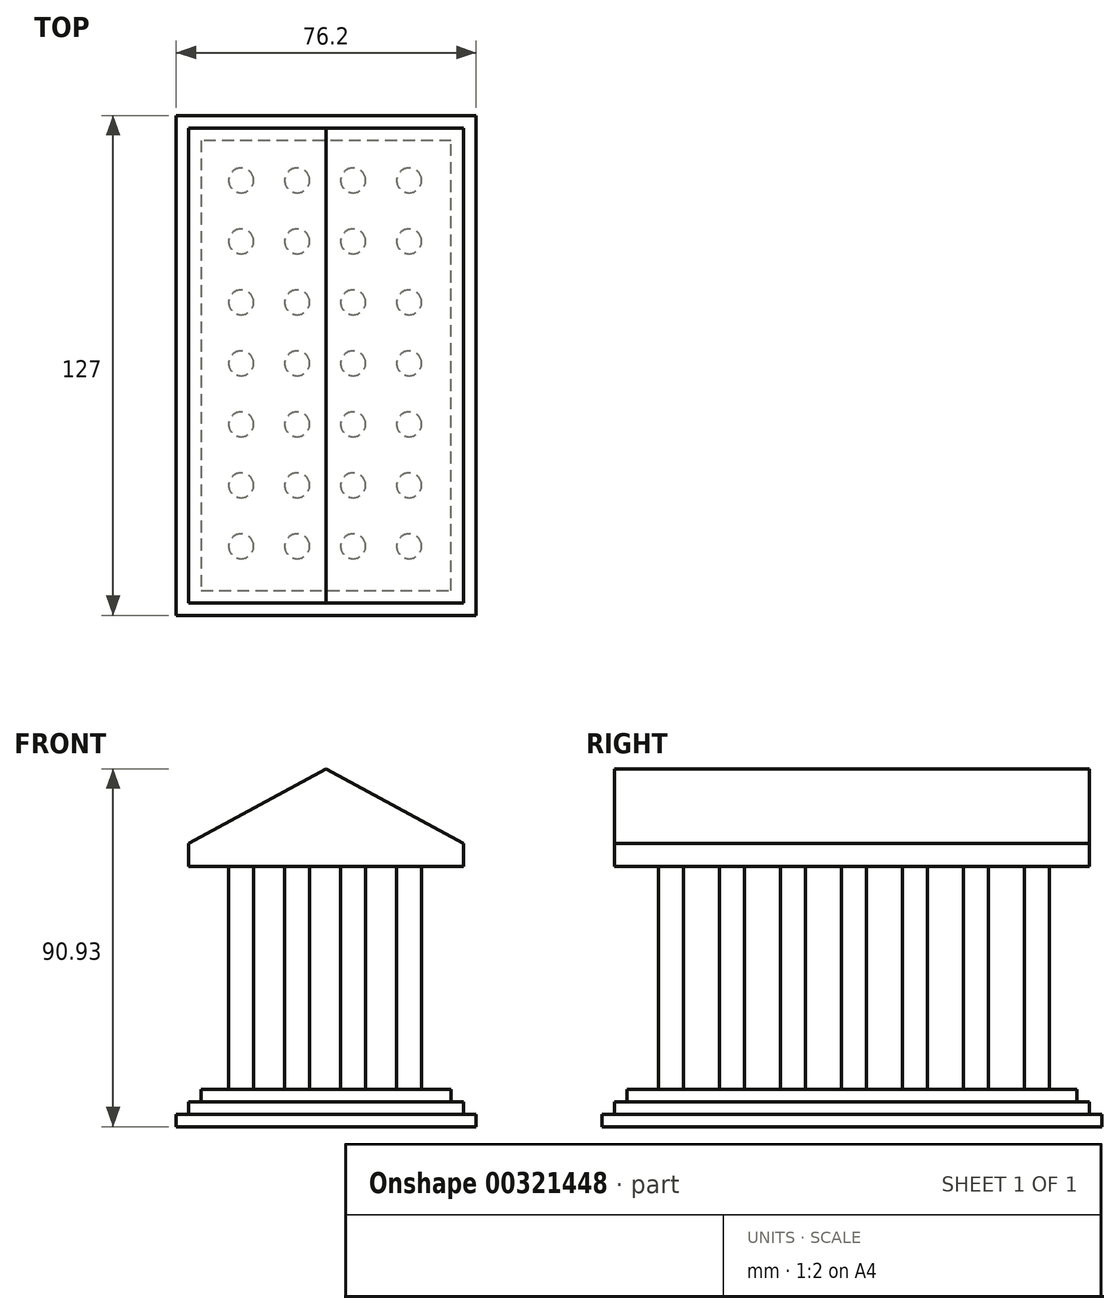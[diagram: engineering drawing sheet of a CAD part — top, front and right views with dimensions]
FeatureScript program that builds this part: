
annotation { "Feature Type Name" : "Feature", "Feature Type Description" : "" }
export const myFeature = defineFeature(function(context is Context, id is Id, definition is map)
    precondition{}
    {
        {
            var Q0;
            Q0=qCreatedBy(makeId("Top.planeOp"),FACE);
            var sketch = newSketch(context, id + "F0", { "sketchPlane" : qUnion([Q0])});
            skLineSegment(sketch, "E0.bottom", {"start": v(38.1, -63.5) * mm, "end": v(-38.1, -63.5) * mm});
            skLineSegment(sketch, "E0.top", {"start": v(38.1, 63.5) * mm, "end": v(-38.1, 63.5) * mm});
            skLineSegment(sketch, "E0.left", {"start": v(38.1, -63.5) * mm, "end": v(38.1, 63.5) * mm});
            skLineSegment(sketch, "E0.right", {"start": v(-38.1, -63.5) * mm, "end": v(-38.1, 63.5) * mm});
            skPoint(sketch, "E0.middle", {"position": v(0, 0) * mm});
            skSolve(sketch);
        }
        {
            var Q0;
            Q0 = qSketchRegion(id + "F0", true);
            extrude(context, id + "F1", {"entities" : qUnion([Q0]), "depth" : 3.17 * mm});
        }
        {
            var Q0;
            Q0=makeQuery(id+"F1.opExtrude","CAP_FACE",FACE,{"disambiguationData":[OSD([sQuery(id+"F0.wireOp",EDGE,"E0.bottom"),sQuery(id+"F0.wireOp",EDGE,"E0.top"),sQuery(id+"F0.wireOp",EDGE,"E0.left"),sQuery(id+"F0.wireOp",EDGE,"E0.right")])],"isStart":false});
            var sketch = newSketch(context, id + "F2", { "sketchPlane" : qUnion([Q0])});
            skLineSegment(sketch, "E1.bottom", {"start": v(34.92, -60.33) * mm, "end": v(-34.92, -60.33) * mm});
            skLineSegment(sketch, "E1.top", {"start": v(34.92, 60.33) * mm, "end": v(-34.92, 60.33) * mm});
            skLineSegment(sketch, "E1.left", {"start": v(34.92, -60.33) * mm, "end": v(34.92, 60.33) * mm});
            skLineSegment(sketch, "E1.right", {"start": v(-34.92, -60.33) * mm, "end": v(-34.92, 60.33) * mm});
            skPoint(sketch, "E1.middle", {"position": v(0, 0) * mm});
            skSolve(sketch);
        }
        {
            var Q0;
            Q0 = qSketchRegion(id + "F2", true);
            extrude(context, id + "F3", {"entities" : qUnion([Q0]), "operationType" : NewBodyOperationType.ADD, "depth" : 3.17 * mm});
        }
        {
            var Q0;
            Q0=makeQuery(id+"F3.opExtrude","CAP_FACE",FACE,{"disambiguationData":[OSD([sQuery(id+"F2.wireOp",EDGE,"E1.bottom"),sQuery(id+"F2.wireOp",EDGE,"E1.top"),sQuery(id+"F2.wireOp",EDGE,"E1.left"),sQuery(id+"F2.wireOp",EDGE,"E1.right")])],"isStart":false});
            var sketch = newSketch(context, id + "F4", { "sketchPlane" : qUnion([Q0])});
            skLineSegment(sketch, "E2.0", {"start": v(31.75, -57.15) * mm, "end": v(31.75, 57.15) * mm});
            skLineSegment(sketch, "E2.1", {"start": v(-31.75, -57.15) * mm, "end": v(31.75, -57.15) * mm});
            skLineSegment(sketch, "E2.2", {"start": v(-31.75, 57.15) * mm, "end": v(-31.75, -57.15) * mm});
            skLineSegment(sketch, "E2.3", {"start": v(31.75, 57.15) * mm, "end": v(-31.75, 57.15) * mm});
            skSolve(sketch);
        }
        {
            var Q0;
            Q0=makeQuery(id+"F4.imprint","IMPRINT",FACE,{"disambiguationData":[TD([[makeQuery(id+"F4.imprint","IMPRINT",EDGE,{"derivedFrom":sQuery(id+"F4.wireOp",EDGE,"E2.0")}),1.0]])]});
            extrude(context, id + "F5", {"entities" : qUnion([Q0]), "operationType" : NewBodyOperationType.ADD, "depth" : 3.17 * mm});
        }
        {
            var Q0;
            Q0=makeQuery(id+"F5.opExtrude","CAP_FACE",FACE,{"disambiguationData":[OSD([sQuery(id+"F4.wireOp",EDGE,"E2.0"),sQuery(id+"F4.wireOp",EDGE,"E2.1"),sQuery(id+"F4.wireOp",EDGE,"E2.2"),sQuery(id+"F4.wireOp",EDGE,"E2.3")])],"isStart":false});
            var sketch = newSketch(context, id + "F6", { "sketchPlane" : qUnion([Q0])});
            skCircle(sketch, "E3", {"center": v(-21.59, 47) * mm, "radius": 3.18 * mm});
            skCircle(sketch, "E4.0.1.0", {"center": v(-21.59, 31.5) * mm, "radius": 3.18 * mm});
            skCircle(sketch, "E4.0.2.0", {"center": v(-21.59, 16) * mm, "radius": 3.18 * mm});
            skCircle(sketch, "E4.0.3.0", {"center": v(-21.59, 0.5) * mm, "radius": 3.18 * mm});
            skCircle(sketch, "E4.0.4.0", {"center": v(-21.59, -14.99) * mm, "radius": 3.18 * mm});
            skCircle(sketch, "E4.0.5.0", {"center": v(-21.59, -30.48) * mm, "radius": 3.18 * mm});
            skCircle(sketch, "E4.0.6.0", {"center": v(-21.59, -45.97) * mm, "radius": 3.18 * mm});
            skCircle(sketch, "E4.1.0.0", {"center": v(-7.37, 47) * mm, "radius": 3.18 * mm});
            skCircle(sketch, "E4.1.1.0", {"center": v(-7.37, 31.5) * mm, "radius": 3.18 * mm});
            skCircle(sketch, "E4.1.2.0", {"center": v(-7.37, 16) * mm, "radius": 3.18 * mm});
            skCircle(sketch, "E4.1.3.0", {"center": v(-7.37, 0.5) * mm, "radius": 3.18 * mm});
            skCircle(sketch, "E4.1.4.0", {"center": v(-7.37, -14.99) * mm, "radius": 3.18 * mm});
            skCircle(sketch, "E4.1.5.0", {"center": v(-7.37, -30.48) * mm, "radius": 3.18 * mm});
            skCircle(sketch, "E4.1.6.0", {"center": v(-7.37, -45.97) * mm, "radius": 3.18 * mm});
            skCircle(sketch, "E4.2.0.0", {"center": v(6.86, 47) * mm, "radius": 3.18 * mm});
            skCircle(sketch, "E4.2.1.0", {"center": v(6.86, 31.5) * mm, "radius": 3.18 * mm});
            skCircle(sketch, "E4.2.2.0", {"center": v(6.86, 16) * mm, "radius": 3.18 * mm});
            skCircle(sketch, "E4.2.3.0", {"center": v(6.86, 0.5) * mm, "radius": 3.18 * mm});
            skCircle(sketch, "E4.2.4.0", {"center": v(6.86, -14.99) * mm, "radius": 3.18 * mm});
            skCircle(sketch, "E4.2.5.0", {"center": v(6.86, -30.48) * mm, "radius": 3.18 * mm});
            skCircle(sketch, "E4.2.6.0", {"center": v(6.86, -45.97) * mm, "radius": 3.18 * mm});
            skCircle(sketch, "E4.3.0.0", {"center": v(21.08, 47) * mm, "radius": 3.18 * mm});
            skCircle(sketch, "E4.3.1.0", {"center": v(21.08, 31.5) * mm, "radius": 3.18 * mm});
            skCircle(sketch, "E4.3.2.0", {"center": v(21.08, 16) * mm, "radius": 3.18 * mm});
            skCircle(sketch, "E4.3.3.0", {"center": v(21.08, 0.5) * mm, "radius": 3.18 * mm});
            skCircle(sketch, "E4.3.4.0", {"center": v(21.08, -14.99) * mm, "radius": 3.18 * mm});
            skCircle(sketch, "E4.3.5.0", {"center": v(21.08, -30.48) * mm, "radius": 3.18 * mm});
            skCircle(sketch, "E4.3.6.0", {"center": v(21.08, -45.97) * mm, "radius": 3.18 * mm});
            skLineSegment(sketch, "E4.direction1", {"start": v(-21.59, 47) * mm, "end": v(-7.37, 47) * mm, "construction": true});
            skLineSegment(sketch, "E4.direction2", {"start": v(-21.59, 47) * mm, "end": v(-21.59, 31.5) * mm, "construction": true});
            skSolve(sketch);
        }
        {
            var Q0;
            Q0 = qSketchRegion(id + "F6", true);
            extrude(context, id + "F7", {"entities" : qUnion([Q0]), "operationType" : NewBodyOperationType.ADD, "depth" : 56.64 * mm});
        }
        {
            var Q0;
            Q0=makeQuery(id+"F7.opExtrude","CAP_FACE",FACE,{"disambiguationData":[OSD([sQuery(id+"F6.wireOp",EDGE,"E4.3.2.0")])],"isStart":false});
            var sketch = newSketch(context, id + "F8", { "sketchPlane" : qUnion([Q0])});
            skLineSegment(sketch, "E5.0", {"start": v(-34.92, -60.33) * mm, "end": v(-34.92, 60.33) * mm});
            skLineSegment(sketch, "E6.0", {"start": v(34.92, -60.33) * mm, "end": v(-34.92, -60.33) * mm});
            skLineSegment(sketch, "E7.0", {"start": v(34.92, -60.33) * mm, "end": v(34.92, 60.33) * mm});
            skLineSegment(sketch, "E8.0", {"start": v(34.92, 60.33) * mm, "end": v(-34.92, 60.33) * mm});
            skSolve(sketch);
        }
        {
            var Q0;
            Q0 = qSketchRegion(id + "F8", true);
            extrude(context, id + "F9", {"entities" : qUnion([Q0]), "operationType" : NewBodyOperationType.ADD, "depth" : 3.17 * mm});
        }
        {
            var Q0;
            Q0=makeQuery(id+"F9.opExtrude","CAP_FACE",FACE,{"disambiguationData":[OSD([sQuery(id+"F8.wireOp",EDGE,"E5.0"),sQuery(id+"F8.wireOp",EDGE,"E6.0"),sQuery(id+"F8.wireOp",EDGE,"E7.0"),sQuery(id+"F8.wireOp",EDGE,"E8.0")])],"isStart":false});
            extrude(context, id + "F10", {"entities" : qUnion([Q0]), "operationType" : NewBodyOperationType.ADD, "depth" : 21.59 * mm});
        }
        {
            var Q0;
            {var subQ0=sQuery(id+"F8.wireOp",EDGE,"E6.0");Q0=makeQuery(id+"F10.boolean.opBoolean","MERGE",FACE,{"derivedFrom":[makeQuery(id+"F9.opExtrude","SWEPT_FACE",FACE,{"disambiguationData":[OSD([subQ0])]}),makeQuery(id+"F10.opExtrude","SWEPT_FACE",FACE,{"disambiguationData":[OSD([subQ0])]})]});}
            var sketch = newSketch(context, id + "F11", { "sketchPlane" : qUnion([Q0])});
            skLineSegment(sketch, "E9", {"start": v(0, 90.93) * mm, "end": v(0, 66.17) * mm, "construction": true});
            skLineSegment(sketch, "E10", {"start": v(0, 90.93) * mm, "end": v(34.92, 71.97) * mm});
            skLineSegment(sketch, "E11", {"start": v(34.92, 71.97) * mm, "end": v(34.92, 90.93) * mm});
            skLineSegment(sketch, "E12", {"start": v(34.92, 90.93) * mm, "end": v(0, 90.93) * mm});
            skLineSegment(sketch, "E13.MirrorCS", {"start": v(0, 90.93) * mm, "end": v(-34.92, 71.97) * mm});
            skLineSegment(sketch, "E14.MirrorCS", {"start": v(-34.92, 71.97) * mm, "end": v(-34.92, 90.93) * mm});
            skLineSegment(sketch, "E15.MirrorCS", {"start": v(-34.92, 90.93) * mm, "end": v(0, 90.93) * mm});
            skSolve(sketch);
        }
        {
            var Q0;
            Q0 = qSketchRegion(id + "F11", true);
            extrude(context, id + "F12", {"entities" : qUnion([Q0]), "operationType" : NewBodyOperationType.REMOVE, "endBound" : BoundingType.THROUGH_ALL, "oppositeDirection" : true, "depth" : 25.4 * mm});
        }
    });
